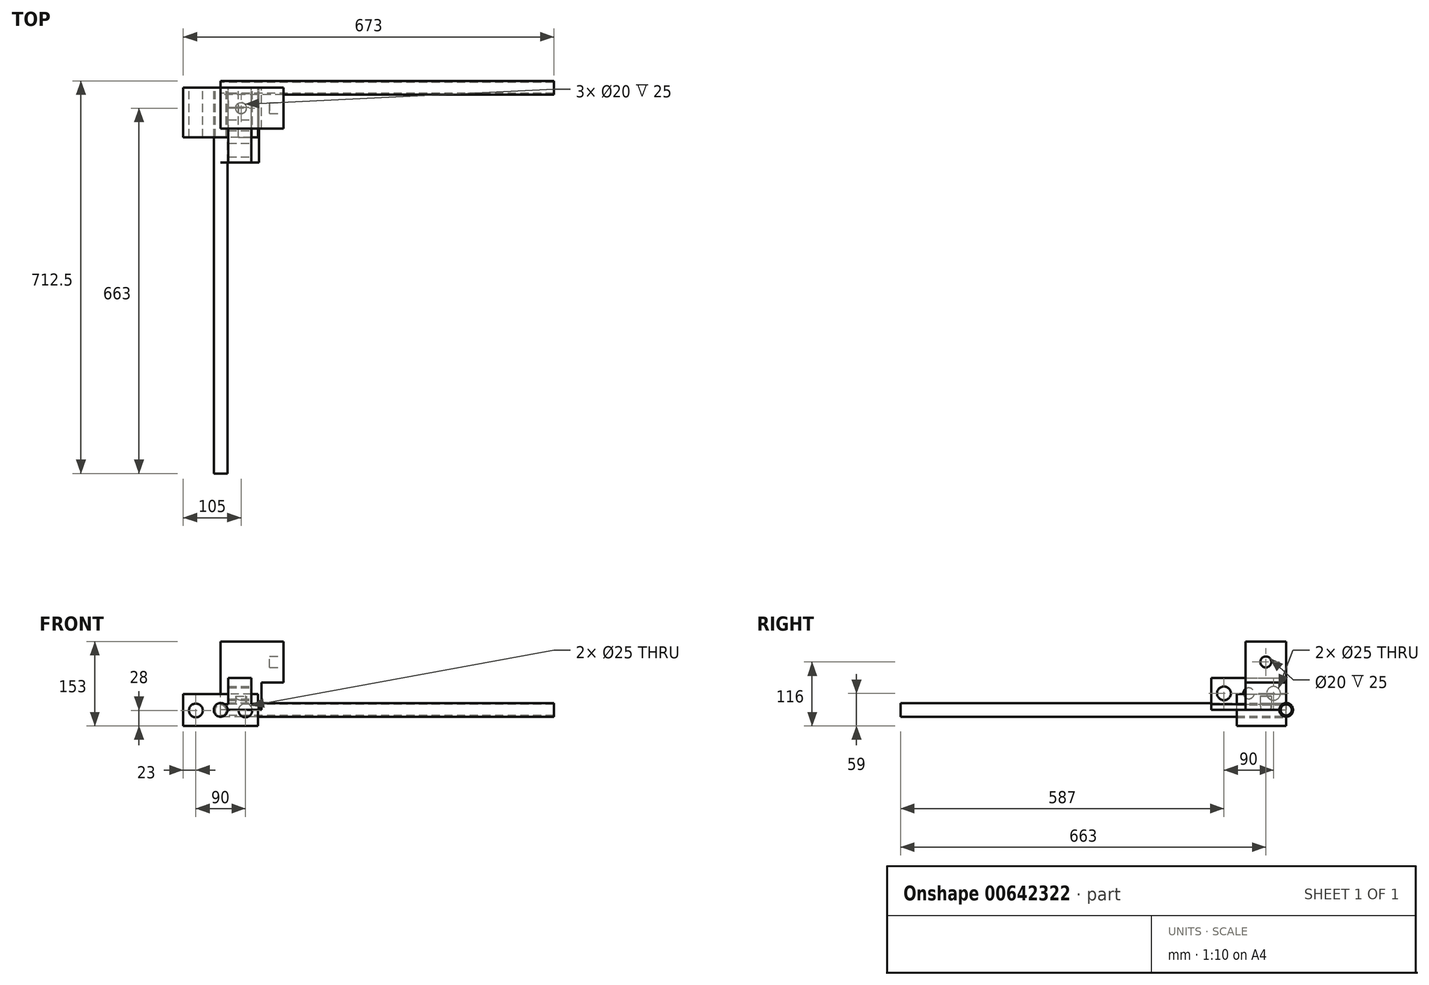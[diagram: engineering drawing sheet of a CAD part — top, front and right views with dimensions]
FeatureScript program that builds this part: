
annotation { "Feature Type Name" : "Feature", "Feature Type Description" : "" }
export const myFeature = defineFeature(function(context is Context, id is Id, definition is map)
    precondition{}
    {
        {
            var Q0;
            Q0=qCreatedBy(makeId("Front.planeOp"),FACE);
            var sketch = newSketch(context, id + "F0", { "sketchPlane" : qUnion([Q0])});
            skLineSegment(sketch, "E0", {"start": v(0, 0) * mm, "end": v(0, 10) * mm});
            skLineSegment(sketch, "E1", {"start": v(0, 10) * mm, "end": v(14, 10) * mm});
            skLineSegment(sketch, "E2", {"start": v(14, 10) * mm, "end": v(14, 58) * mm});
            skLineSegment(sketch, "E3", {"start": v(14, 58) * mm, "end": v(56, 58) * mm});
            skLineSegment(sketch, "E4", {"start": v(56, 58) * mm, "end": v(56, 10) * mm});
            skLineSegment(sketch, "E5", {"start": v(56, 10) * mm, "end": v(70, 10) * mm});
            skLineSegment(sketch, "E6", {"start": v(70, 10) * mm, "end": v(70, 0) * mm});
            skLineSegment(sketch, "E7", {"start": v(70, 0) * mm, "end": v(0, 0) * mm});
            skSolve(sketch);
        }
        {
            var Q0;
            Q0=makeQuery(id+"F0.imprint","IMPRINT",FACE,{"disambiguationData":[TD([[makeQuery(id+"F0.imprint","IMPRINT",EDGE,{"derivedFrom":sQuery(id+"F0.wireOp",EDGE,"E0")}),-1.0]])]});
            extrude(context, id + "F1", {"entities" : qUnion([Q0]), "depth" : 136 * mm, "offsetDistance" : 25 * mm});
        }
        {
            var Q0;
            Q0=makeQuery(id+"F1.opExtrude","SWEPT_FACE",FACE,{"disambiguationData":[OSD([sQuery(id+"F0.wireOp",EDGE,"E4")])]});
            var sketch = newSketch(context, id + "F2", { "sketchPlane" : qUnion([Q0])});
            skCircle(sketch, "E8", {"center": v(-68, 30) * mm, "radius": 10 * mm});
            skCircle(sketch, "E9", {"center": v(-113, 30) * mm, "radius": 12.5 * mm});
            skCircle(sketch, "E10", {"center": v(-23, 30) * mm, "radius": 12.5 * mm});
            skLineSegment(sketch, "E11", {"start": v(-113, 30) * mm, "end": v(-68, 30) * mm, "construction": true});
            skLineSegment(sketch, "E12", {"start": v(-23, 30) * mm, "end": v(-68, 30) * mm, "construction": true});
            skLineSegment(sketch, "E13", {"start": v(-113, 30) * mm, "end": v(-136, 30) * mm, "construction": true});
            skLineSegment(sketch, "E14", {"start": v(-23, 30) * mm, "end": v(0, 30) * mm, "construction": true});
            skSolve(sketch);
        }
        {
            var Q0;
            Q0=makeQuery(id+"F2.imprint","IMPRINT",FACE,{"disambiguationData":[TD([[makeQuery(id+"F2.imprint","IMPRINT",EDGE,{"derivedFrom":sQuery(id+"F2.wireOp",EDGE,"E9")}),1.0]])]});
            var Q1;
            Q1=makeQuery(id+"F2.imprint","IMPRINT",FACE,{"disambiguationData":[TD([[makeQuery(id+"F2.imprint","IMPRINT",EDGE,{"derivedFrom":sQuery(id+"F2.wireOp",EDGE,"E8")}),1.0]])]});
            var Q2;
            Q2=makeQuery(id+"F2.imprint","IMPRINT",FACE,{"disambiguationData":[TD([[makeQuery(id+"F2.imprint","IMPRINT",EDGE,{"derivedFrom":sQuery(id+"F2.wireOp",EDGE,"E10")}),1.0]])]});
            extrude(context, id + "F3", {"entities" : qUnion([Q0, Q1, Q2]), "operationType" : NewBodyOperationType.REMOVE, "endBound" : BoundingType.THROUGH_ALL, "oppositeDirection" : true, "depth" : 25 * mm, "offsetDistance" : 25 * mm});
        }
        {
            var Q0;
            Q0=qCreatedBy(makeId("Right.planeOp"),FACE);
            var sketch = newSketch(context, id + "F4", { "sketchPlane" : qUnion([Q0])});
            skCircle(sketch, "E15", {"center": v(0, 0) * mm, "radius": 10 * mm});
            skCircle(sketch, "E16", {"center": v(0, 0) * mm, "radius": 12.5 * mm});
            skSolve(sketch);
        }
        {
            var Q0;
            Q0=makeQuery(id+"F4.imprint","IMPRINT",FACE,{"disambiguationData":[TD([[makeQuery(id+"F4.imprint","IMPRINT",EDGE,{"derivedFrom":sQuery(id+"F4.wireOp",EDGE,"E15")}),1.0]])]});
            extrude(context, id + "F5", {"entities" : qUnion([Q0]), "depth" : (305 + 300) * mm, "offsetDistance" : 25 * mm});
        }
        {
            var Q0;
            Q0=makeQuery(id+"F4.imprint","IMPRINT",FACE,{"disambiguationData":[TD([[makeQuery(id+"F4.imprint","IMPRINT",EDGE,{"derivedFrom":sQuery(id+"F4.wireOp",EDGE,"E15")}),-1.0]])]});
            var Q1;
            Q1=makeQuery(id+"F4.imprint","IMPRINT",FACE,{"disambiguationData":[TD([[makeQuery(id+"F4.imprint","IMPRINT",EDGE,{"derivedFrom":sQuery(id+"F4.wireOp",EDGE,"E15")}),1.0]])]});
            extrude(context, id + "F6", {"entities" : qUnion([Q0, Q1]), "depth" : (305 + 300) * mm, "offsetDistance" : 25 * mm});
        }
        {
            var Q0;
            Q0=qCreatedBy(makeId("Front.planeOp"),FACE);
            var sketch = newSketch(context, id + "F7", { "sketchPlane" : qUnion([Q0])});
            skLineSegment(sketch, "E17.bottom", {"start": v(68, -29) * mm, "end": v(-68, -29) * mm});
            skLineSegment(sketch, "E17.top", {"start": v(68, 29) * mm, "end": v(-68, 29) * mm});
            skLineSegment(sketch, "E17.left", {"start": v(68, -29) * mm, "end": v(68, 29) * mm});
            skLineSegment(sketch, "E17.right", {"start": v(-68, -29) * mm, "end": v(-68, 29) * mm});
            skPoint(sketch, "E17.middle", {"position": v(0, 0) * mm});
            skCircle(sketch, "E18", {"center": v(-45, -1) * mm, "radius": 12.5 * mm});
            skCircle(sketch, "E19", {"center": v(0, -1) * mm, "radius": 10 * mm});
            skCircle(sketch, "E20", {"center": v(45, -1) * mm, "radius": 12.5 * mm});
            skLineSegment(sketch, "E21", {"start": v(-68, -1) * mm, "end": v(-45, -1) * mm, "construction": true});
            skLineSegment(sketch, "E22", {"start": v(0, -1) * mm, "end": v(-45, -1) * mm, "construction": true});
            skLineSegment(sketch, "E23", {"start": v(0, -1) * mm, "end": v(45, -1) * mm, "construction": true});
            skLineSegment(sketch, "E24", {"start": v(45, -1) * mm, "end": v(68, -1) * mm, "construction": true});
            skSolve(sketch);
        }
        {
            var Q0;
            Q0=makeQuery(id+"F7.imprint","IMPRINT",FACE,{"disambiguationData":[TD([[makeQuery(id+"F7.imprint","IMPRINT",EDGE,{"derivedFrom":sQuery(id+"F7.wireOp",EDGE,"E17.bottom")}),-1.0]])]});
            extrude(context, id + "F8", {"entities" : qUnion([Q0]), "depth" : 90 * mm, "offsetDistance" : 25 * mm});
        }
        {
            var Q0;
            Q0=qCreatedBy(makeId("Front.planeOp"),FACE);
            var sketch = newSketch(context, id + "F9", { "sketchPlane" : qUnion([Q0])});
            skLineSegment(sketch, "E25", {"start": v(0, 0) * mm, "end": v(0, 124) * mm});
            skLineSegment(sketch, "E26", {"start": v(0, 124) * mm, "end": v(114, 124) * mm});
            skLineSegment(sketch, "E27", {"start": v(114, 124) * mm, "end": v(114, 50) * mm});
            skLineSegment(sketch, "E28", {"start": v(114, 50) * mm, "end": v(74, 50) * mm});
            skLineSegment(sketch, "E29", {"start": v(74, 50) * mm, "end": v(74, 0) * mm});
            skLineSegment(sketch, "E30", {"start": v(74, 0) * mm, "end": v(0, 0) * mm});
            skSolve(sketch);
        }
        {
            var Q0;
            Q0=makeQuery(id+"F9.imprint","IMPRINT",FACE,{"disambiguationData":[TD([[makeQuery(id+"F9.imprint","IMPRINT",EDGE,{"derivedFrom":sQuery(id+"F9.wireOp",EDGE,"E25")}),-1.0]])]});
            extrude(context, id + "F10", {"entities" : qUnion([Q0]), "depth" : 74 * mm, "offsetDistance" : 25 * mm});
        }
        {
            var Q0;
            Q0=makeQuery(id+"F10.opExtrude","SWEPT_FACE",FACE,{"disambiguationData":[OSD([sQuery(id+"F9.wireOp",EDGE,"E30")])]});
            var sketch = newSketch(context, id + "F11", { "sketchPlane" : qUnion([Q0])});
            skCircle(sketch, "E31", {"center": v(37, 37) * mm, "radius": 10 * mm});
            skPoint(sketch, "E31.centerSnap0", {"position": v(0, 37) * mm});
            skPoint(sketch, "E31.centerSnap1", {"position": v(37, 74) * mm});
            skSolve(sketch);
        }
        {
            var Q0;
            Q0=makeQuery(id+"F11.imprint","IMPRINT",FACE,{"disambiguationData":[TD([[makeQuery(id+"F11.imprint","IMPRINT",EDGE,{"derivedFrom":sQuery(id+"F11.wireOp",EDGE,"E31")}),1.0]])]});
            extrude(context, id + "F12", {"entities" : qUnion([Q0]), "operationType" : NewBodyOperationType.REMOVE, "oppositeDirection" : true, "depth" : 25 * mm, "offsetDistance" : 25 * mm});
        }
        {
            var Q0;
            Q0=makeQuery(id+"F10.opExtrude","SWEPT_FACE",FACE,{"disambiguationData":[OSD([sQuery(id+"F9.wireOp",EDGE,"E27")])]});
            var sketch = newSketch(context, id + "F13", { "sketchPlane" : qUnion([Q0])});
            skCircle(sketch, "E32", {"center": v(-37, 87) * mm, "radius": 10 * mm});
            skPoint(sketch, "E32.centerSnap0", {"position": v(-37, 124) * mm});
            skPoint(sketch, "E32.centerSnap1", {"position": v(-74, 87) * mm});
            skSolve(sketch);
        }
        {
            var Q0;
            Q0=makeQuery(id+"F13.imprint","IMPRINT",FACE,{"disambiguationData":[TD([[makeQuery(id+"F13.imprint","IMPRINT",EDGE,{"derivedFrom":sQuery(id+"F13.wireOp",EDGE,"E32")}),1.0]])]});
            extrude(context, id + "F14", {"entities" : qUnion([Q0]), "operationType" : NewBodyOperationType.REMOVE, "oppositeDirection" : true, "depth" : 25 * mm, "offsetDistance" : 25 * mm});
        }
        {
            var Q0;
            Q0=qCreatedBy(makeId("Front.planeOp"),FACE);
            var sketch = newSketch(context, id + "F15", { "sketchPlane" : qUnion([Q0])});
            skCircle(sketch, "E33", {"center": v(0, 0) * mm, "radius": 12.5 * mm});
            skSolve(sketch);
        }
        {
            var Q0;
            Q0=makeQuery(id+"F15.imprint","IMPRINT",FACE,{"disambiguationData":[TD([[makeQuery(id+"F15.imprint","IMPRINT",EDGE,{"derivedFrom":sQuery(id+"F15.wireOp",EDGE,"E33")}),1.0]])]});
            extrude(context, id + "F16", {"entities" : qUnion([Q0]), "depth" : 700 * mm, "offsetDistance" : 25 * mm});
        }
    });
